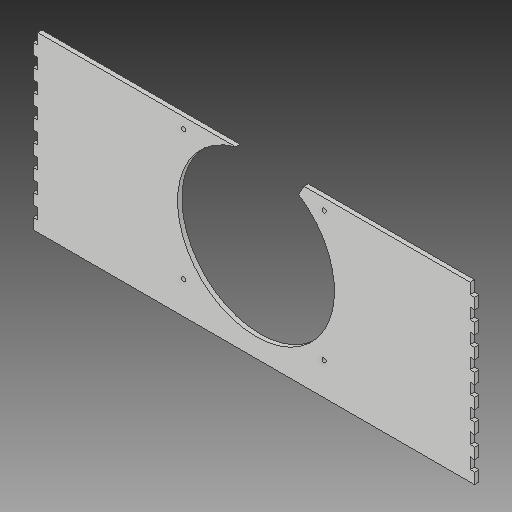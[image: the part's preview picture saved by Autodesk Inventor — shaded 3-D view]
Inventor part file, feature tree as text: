
AUTODESK INVENTOR PART (.ipt)
format: ipt  version: 2019 (Build 230136000, 136)  size: 205,824 bytes
history: native  units: mm
features: reference x15, other x4, extrude x4, sketch x4
ambient origin geometry x8: Origin, YZ Plane, XZ Plane, XY Plane, X Axis, Y Axis, Z Axis, Center Point
bodies: Body1 (feature_tree)
feature tree (27):
  other  "Твердое тело1"
  extrude  "Выдавливание1"  Depth=140.0mm
  extrude  "Выдавливание2"  Depth=400.0mm
  extrude  "Выдавливание3"  Depth=150.0mm
  extrude  "Выдавливание4"  Depth=125.0mm
  sketch  "Эскиз1"
  reference  "Ссылка1"
  reference  "Ссылка2"
  reference  "Ссылка3"
  reference  "Ссылка4"
  reference  "Ссылка5"
  reference  "Ссылка6"
  reference  "Ссылка7"
  reference  "Ссылка8"
  reference  "Ссылка9"
  reference  "Ссылка10"
  sketch  "Эскиз2"
  reference  "Ссылка11"
  sketch  "Эскиз3"
  sketch  "Эскиз4"
  reference  "Ссылка12"
  reference  "Ссылка13"
  reference  "Ссылка14"
  reference  "Ссылка15"
  parser-record x1  (decoder bookkeeping rows leaked as tree rows — omitted from the tree; the rows remain in map.json)
  other  "kowsh.iam"
  other  "mot37:1"
note: 1 file-system path scrubbed to <path> (originals preserved in map.json)
